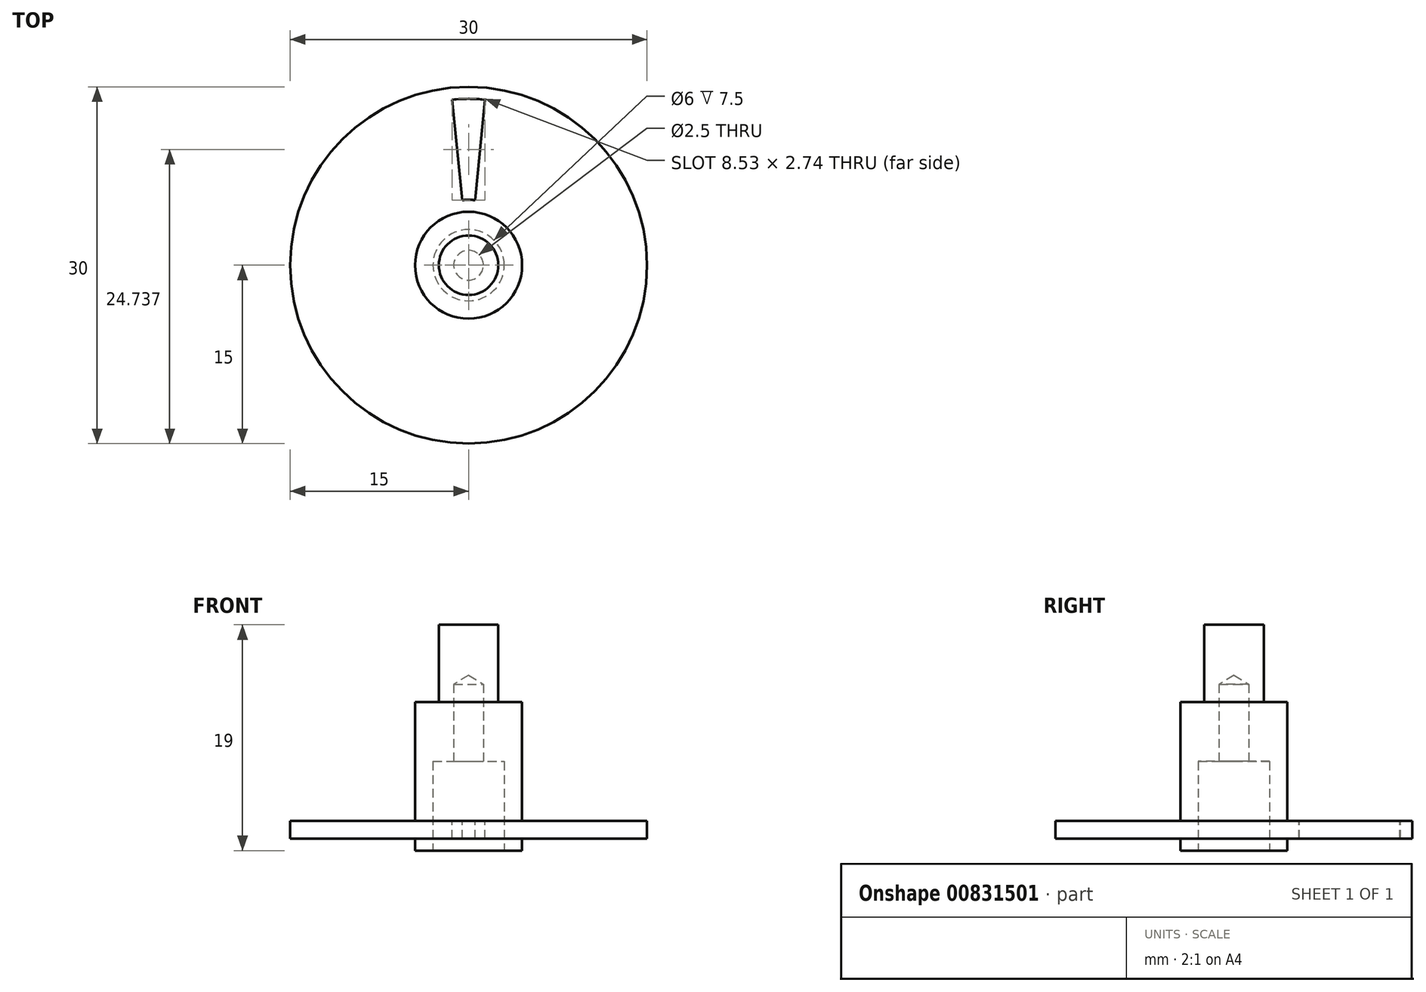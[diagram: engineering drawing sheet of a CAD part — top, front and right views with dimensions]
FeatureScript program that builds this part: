
annotation { "Feature Type Name" : "Feature", "Feature Type Description" : "" }
export const myFeature = defineFeature(function(context is Context, id is Id, definition is map)
    precondition{}
    {
        {
            var Q0;
            Q0=qCreatedBy(makeId("Front.planeOp"),FACE);
            var sketch = newSketch(context, id + "F0", { "sketchPlane" : qUnion([Q0])});
            skLineSegment(sketch, "E0", {"start": v(-3, 0) * mm, "end": v(-3, 7.5) * mm});
            skLineSegment(sketch, "E1", {"start": v(-3, 7.5) * mm, "end": v(0, 7.5) * mm});
            skLineSegment(sketch, "E2", {"start": v(0, 7.5) * mm, "end": v(0, 19) * mm});
            skLineSegment(sketch, "E3", {"start": v(0, 19) * mm, "end": v(-2.5, 19) * mm});
            skLineSegment(sketch, "E4", {"start": v(-2.5, 19) * mm, "end": v(-2.5, 12.5) * mm});
            skLineSegment(sketch, "E5", {"start": v(-2.5, 12.5) * mm, "end": v(-4.5, 12.5) * mm});
            skLineSegment(sketch, "E6", {"start": v(-4.5, 12.5) * mm, "end": v(-4.5, 2.5) * mm});
            skLineSegment(sketch, "E7", {"start": v(-4.5, 2.5) * mm, "end": v(-15, 2.5) * mm});
            skLineSegment(sketch, "E8", {"start": v(-15, 2.5) * mm, "end": v(-15, 1) * mm});
            skLineSegment(sketch, "E9", {"start": v(-15, 1) * mm, "end": v(-4.5, 1) * mm});
            skLineSegment(sketch, "E10", {"start": v(-4.5, 1) * mm, "end": v(-4.5, 0) * mm});
            skLineSegment(sketch, "E11", {"start": v(-4.5, 0) * mm, "end": v(-3, 0) * mm});
            skLineSegment(sketch, "E12", {"start": v(-4.5, 1) * mm, "end": v(-4.5, 2.5) * mm, "construction": true});
            skLineSegment(sketch, "E13", {"start": v(0, 0) * mm, "end": v(0, 26.37) * mm, "construction": true});
            skSolve(sketch);
        }
        {
            var Q0;
            Q0 = qSketchRegion(id + "F0", true);
            var Q1;
            Q1=sQuery(id+"F0.wireOp",EDGE,"E13");
            revolve(context, id + "F1", {"surfaceOperationType" : NewSurfaceOperationType.NEW, "entities" : qUnion([Q0]), "axis" : qUnion([Q1]), "revolveType" : RevolveType.FULL});
        }
        {
            var Q0;
            Q0=makeQuery(id+"F1.opRevolve","SWEPT_FACE",FACE,{"disambiguationData":[OSD([sQuery(id+"F0.wireOp",EDGE,"E1")])]});
            var sketch = newSketch(context, id + "F2", { "sketchPlane" : qUnion([Q0])});
            skPoint(sketch, "E14", {"position": v(0, 0) * mm});
            skSolve(sketch);
        }
        {
            var Q0;
            Q0=sQuery(id+"F2.wireOp",VERTEX,"E14");
            var Q1;
            Q1=makeQuery(id+"F1.opRevolve","SWEPT_BODY",BODY,{"disambiguationData":[OSD([sQuery(id+"F0.wireOp",EDGE,"E0"),sQuery(id+"F0.wireOp",EDGE,"E1"),sQuery(id+"F0.wireOp",EDGE,"E2"),sQuery(id+"F0.wireOp",EDGE,"E3"),sQuery(id+"F0.wireOp",EDGE,"E4"),sQuery(id+"F0.wireOp",EDGE,"E5"),sQuery(id+"F0.wireOp",EDGE,"E6"),sQuery(id+"F0.wireOp",EDGE,"E7"),sQuery(id+"F0.wireOp",EDGE,"E8"),sQuery(id+"F0.wireOp",EDGE,"E9"),sQuery(id+"F0.wireOp",EDGE,"E10"),sQuery(id+"F0.wireOp",EDGE,"E11")])]});
            hole(context, id + "F3", {"style" : HoleStyle.SIMPLE, "endStyle" : HoleEndStyle.BLIND, "standardTappedOrClearance" : lookupTablePath({ "standard" : "ISO", "engagement" : "75%", "pitch" : "0.5 mm", "size" : "M3", "type" : "Tapped" }), "standardBlindInLast" : lookupTablePath({ "standard" : "ISO", "engagement" : "75%", "pitch" : "0.5 mm", "size" : "M3", "type" : "Tapped" }), "holeDiameter" : 2.5 * mm, "majorDiameter" : 3 * mm, "showTappedDepth" : true, "holeDepth" : 6.5 * mm, "isTappedThrough" : true, "tappedDepth" : 5 * mm, "tapClearance" : 3, "startFromSketch" : true, "locations" : qUnion([Q0]), "scope" : qUnion([Q1])});
        }
        {
            var Q0;
            Q0=makeQuery(id+"F1.opRevolve","SWEPT_FACE",FACE,{"disambiguationData":[OSD([sQuery(id+"F0.wireOp",EDGE,"E7")])]});
            var sketch = newSketch(context, id + "F4", { "sketchPlane" : qUnion([Q0])});
            skLineSegment(sketch, "E15", {"start": v(0, 0) * mm, "end": v(-1.47, 14.93) * mm, "construction": true});
            skLineSegment(sketch, "E16", {"start": v(0, 0) * mm, "end": v(1.47, 14.93) * mm, "construction": true});
            skLineSegment(sketch, "E17", {"start": v(-1.47, 14.93) * mm, "end": v(1.47, 14.93) * mm, "construction": true});
            skLineSegment(sketch, "E18", {"start": v(0, 0) * mm, "end": v(0, 14.93) * mm, "construction": true});
            skArc(sketch, "E19", {"start": v(-0.54, 5.47) * mm, "mid": v(0, 5.5) * mm, "end": v(0.54, 5.47) * mm});
            skArc(sketch, "E20", {"start": v(-1.37, 13.93) * mm, "mid": v(0, 14) * mm, "end": v(1.37, 13.93) * mm});
            skLineSegment(sketch, "E21", {"start": v(-0.54, 5.47) * mm, "end": v(-1.37, 13.93) * mm});
            skLineSegment(sketch, "E22", {"start": v(0.54, 5.47) * mm, "end": v(1.37, 13.93) * mm});
            skSolve(sketch);
        }
        {
            var Q0;
            Q0 = qSketchRegion(id + "F4", true);
            extrude(context, id + "F5", {"entities" : qUnion([Q0]), "operationType" : NewBodyOperationType.REMOVE, "endBound" : BoundingType.THROUGH_ALL, "oppositeDirection" : true, "depth" : 25 * mm, "offsetDistance" : 25 * mm});
        }
    });
